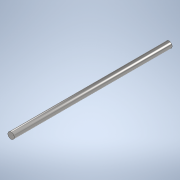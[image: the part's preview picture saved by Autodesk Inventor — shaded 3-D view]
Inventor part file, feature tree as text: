
AUTODESK INVENTOR PART (.ipt)
format: ipt  version: 2020 (Build 240168000, 168)  size: 94,720 bytes
history: native  units: mm
features: extrude x1, sketch x1
ambient origin geometry x8: Origin, YZ Plane, XZ Plane, XY Plane, X Axis, Y Axis, Z Axis, Center Point
bodies: Solid1 (feature_tree)
feature tree (2):
  extrude  "Extrusion1"  Depth=200.0mm TaperAngle=0.0deg
  sketch  "Sketch1"  dims[d0=8.0mm d1=200.0mm d2=0.0mm]
